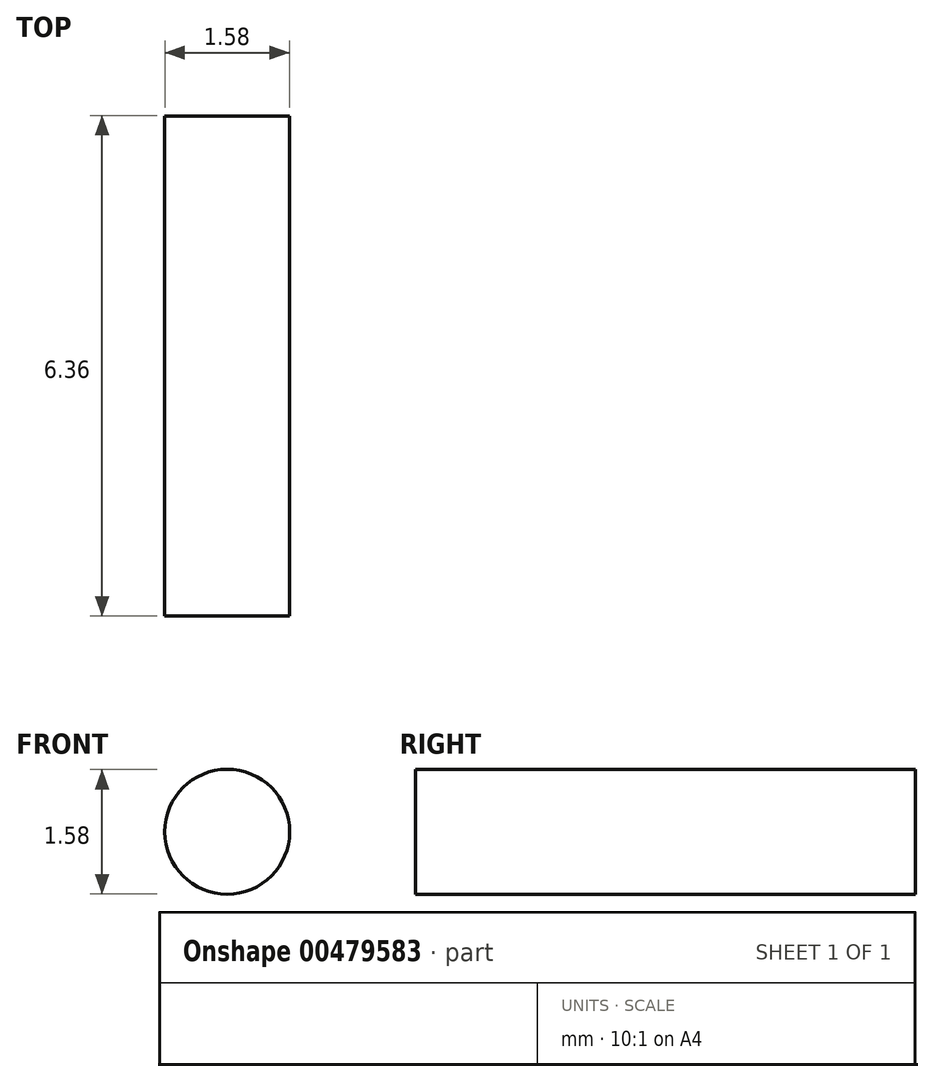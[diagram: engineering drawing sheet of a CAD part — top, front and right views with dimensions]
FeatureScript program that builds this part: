
annotation { "Feature Type Name" : "Feature", "Feature Type Description" : "" }
export const myFeature = defineFeature(function(context is Context, id is Id, definition is map)
    precondition{}
    {
        {
            var Q0;
            Q0=qCreatedBy(makeId("Front.planeOp"),FACE);
            var sketch = newSketch(context, id + "F0", { "sketchPlane" : qUnion([Q0])});
            skCircle(sketch, "E0", {"center": v(0, 0) * mm, "radius": 0.8 * mm});
            skSolve(sketch);
        }
        {
            var Q0;
            Q0=makeQuery(id+"F0.imprint","IMPRINT",FACE,{"disambiguationData":[TD([[makeQuery(id+"F0.imprint","IMPRINT",EDGE,{"derivedFrom":sQuery(id+"F0.wireOp",EDGE,"E0")}),1.0]])]});
            extrude(context, id + "F1", {"entities" : qUnion([Q0]), "depth" : 6.35 * mm, "symmetric" : true});
        }
    });
